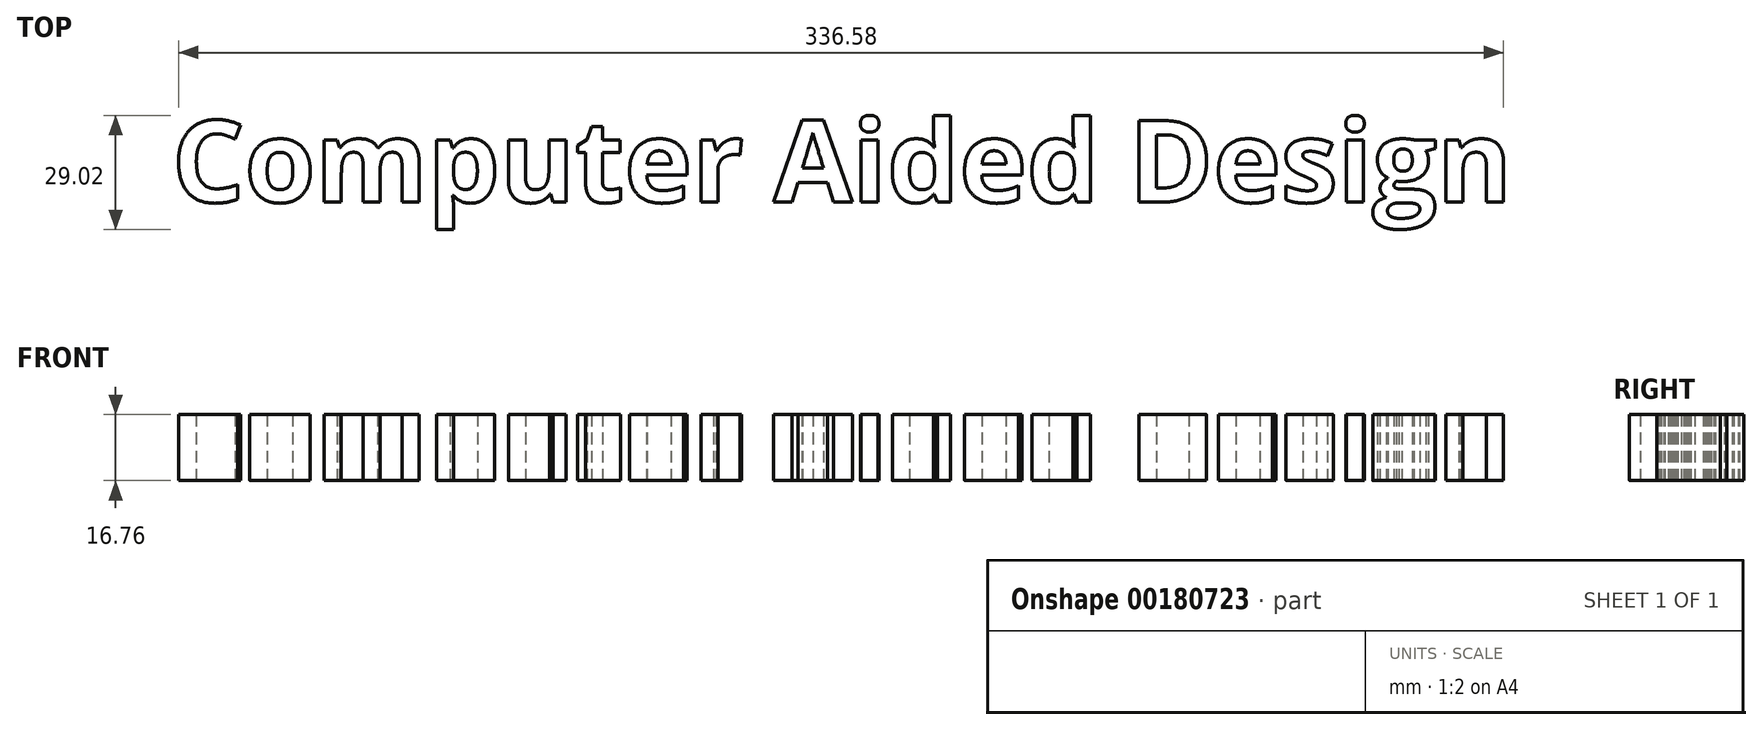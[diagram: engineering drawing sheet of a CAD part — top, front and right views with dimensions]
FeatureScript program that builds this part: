
annotation { "Feature Type Name" : "Feature", "Feature Type Description" : "" }
export const myFeature = defineFeature(function(context is Context, id is Id, definition is map)
    precondition{}
    {
        {
            var Q0;
            Q0=qCreatedBy(makeId("Top.planeOp"),FACE);
            var sketch = newSketch(context, id + "F0", { "sketchPlane" : qUnion([Q0])});
            skText(sketch, "E0", { "text": "Computer Aided Design", "fontName": "OpenSans-Bold.ttf"});
            const initialGuessF0  = {"E0": [-0.34007, 0, 1, 0, 0.02089]};
            skSetInitialGuess(sketch, initialGuessF0);
            skSolve(sketch);
        }
        {
            var Q0;
            Q0 = qConstructionFilter(qBodyType(qCreatedBy(id + "F0" ,EDGE), BodyType.WIRE), ConstructionObject.NO);
            extrude(context, id + "F1", {"bodyType" : ToolBodyType.SURFACE, "operationType" : NewBodyOperationType.ADD, "surfaceEntities" : qUnion([Q0]), "oppositeDirection" : true, "depth" : 16.76 * mm});
        }
    });
